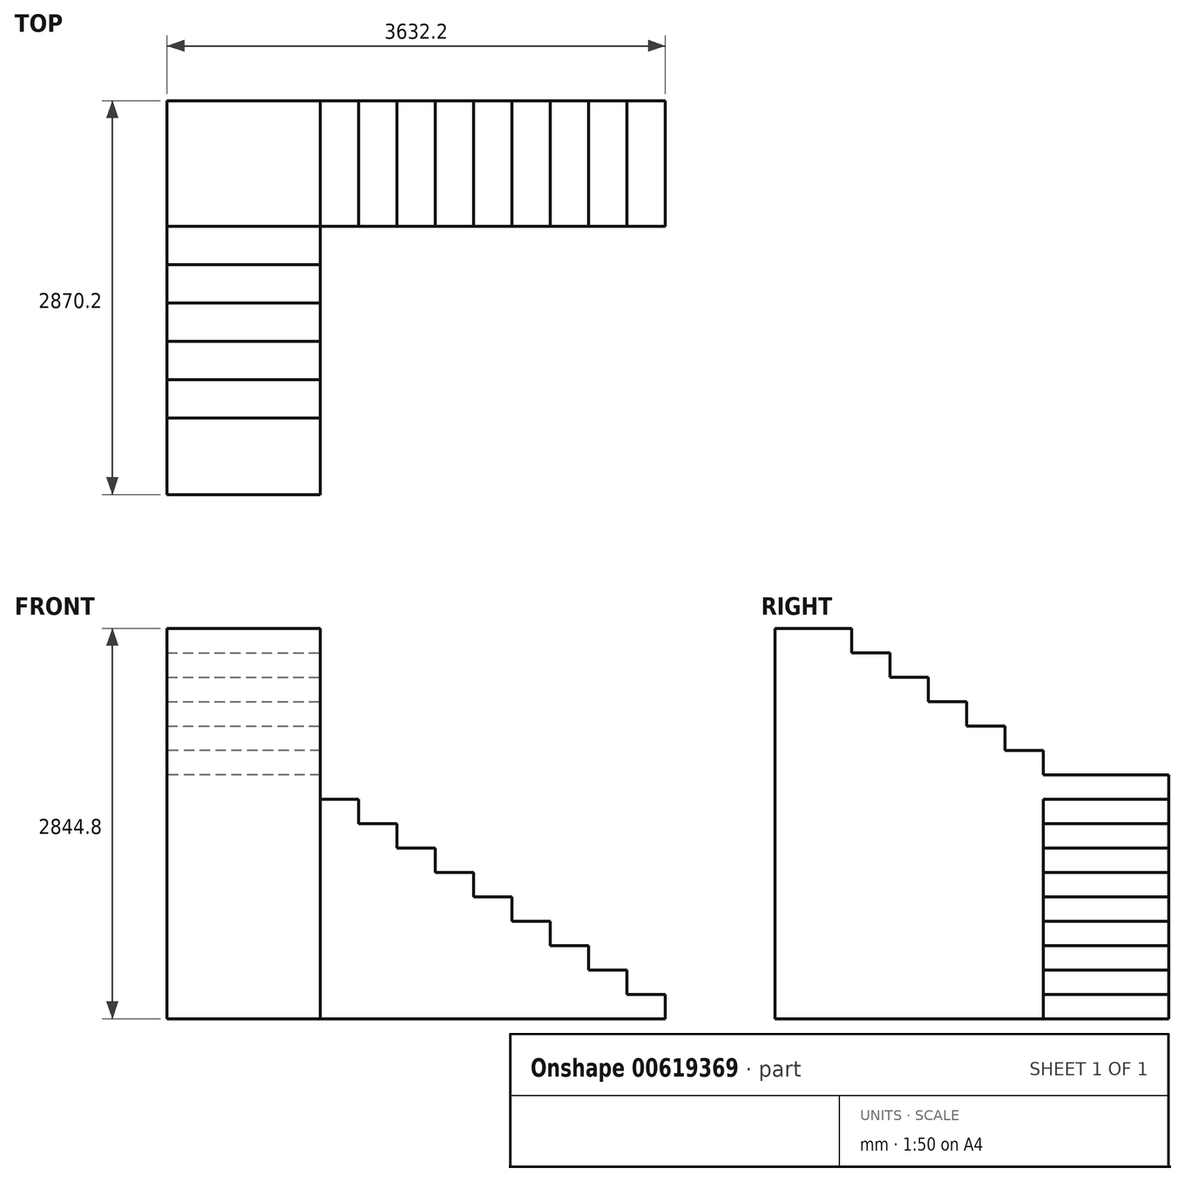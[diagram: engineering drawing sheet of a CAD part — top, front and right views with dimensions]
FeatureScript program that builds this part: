
annotation { "Feature Type Name" : "Feature", "Feature Type Description" : "" }
export const myFeature = defineFeature(function(context is Context, id is Id, definition is map)
    precondition{}
    {
        {
            var Q0;
            Q0=qCreatedBy(makeId("Top.planeOp"),FACE);
            var sketch = newSketch(context, id + "F0", { "sketchPlane" : qUnion([Q0])});
            skLineSegment(sketch, "E0.bottom", {"start": v(0, 0) * mm, "end": v(-2514.6, 0) * mm});
            skLineSegment(sketch, "E0.top", {"start": v(0, 914.4) * mm, "end": v(-2514.6, 914.4) * mm});
            skLineSegment(sketch, "E0.left", {"start": v(0, 0) * mm, "end": v(0, 914.4) * mm});
            skLineSegment(sketch, "E1", {"start": v(-1397, 914.4) * mm, "end": v(-1397, 0) * mm});
            skLineSegment(sketch, "E2", {"start": v(-1955.8, 914.4) * mm, "end": v(-1955.8, 0) * mm});
            skLineSegment(sketch, "E3", {"start": v(-838.2, 914.4) * mm, "end": v(-838.2, 0) * mm});
            skLineSegment(sketch, "E4", {"start": v(-1676.4, 914.4) * mm, "end": v(-1676.4, 0) * mm});
            skLineSegment(sketch, "E5", {"start": v(-279.4, 914.4) * mm, "end": v(-279.4, 0) * mm});
            skLineSegment(sketch, "E6", {"start": v(-1117.6, 914.4) * mm, "end": v(-1117.6, 0) * mm});
            skLineSegment(sketch, "E7", {"start": v(-558.8, 914.4) * mm, "end": v(-558.8, 0) * mm});
            skLineSegment(sketch, "E8", {"start": v(-2235.2, 914.4) * mm, "end": v(-2235.2, 0) * mm});
            skLineSegment(sketch, "E9.bottom", {"start": v(-2514.6, 914.4) * mm, "end": v(-3632.2, 914.4) * mm});
            skLineSegment(sketch, "E9.top", {"start": v(-2514.6, 0) * mm, "end": v(-3632.2, 0) * mm});
            skLineSegment(sketch, "E9.left", {"start": v(-2514.6, 914.4) * mm, "end": v(-2514.6, 0) * mm});
            skLineSegment(sketch, "E9.right", {"start": v(-3632.2, 914.4) * mm, "end": v(-3632.2, 0) * mm});
            skLineSegment(sketch, "E10", {"start": v(-3632.2, 0) * mm, "end": v(-3632.2, -279.4) * mm});
            skLineSegment(sketch, "E11", {"start": v(-3632.2, -279.4) * mm, "end": v(-2514.6, -279.4) * mm});
            skLineSegment(sketch, "E12", {"start": v(-2514.6, -279.4) * mm, "end": v(-2514.6, 0) * mm});
            skLineSegment(sketch, "E13", {"start": v(-3632.2, -279.4) * mm, "end": v(-3632.2, -558.8) * mm});
            skLineSegment(sketch, "E14", {"start": v(-3632.2, -558.8) * mm, "end": v(-2514.6, -558.8) * mm});
            skLineSegment(sketch, "E15", {"start": v(-2514.6, -558.8) * mm, "end": v(-2514.6, -279.4) * mm});
            skLineSegment(sketch, "E16", {"start": v(-3632.2, -558.8) * mm, "end": v(-3632.2, -838.2) * mm});
            skLineSegment(sketch, "E17", {"start": v(-3632.2, -838.2) * mm, "end": v(-2514.6, -838.2) * mm});
            skLineSegment(sketch, "E18", {"start": v(-2514.6, -838.2) * mm, "end": v(-2514.6, -558.8) * mm});
            skLineSegment(sketch, "E19", {"start": v(-3632.2, -838.2) * mm, "end": v(-3632.2, -1117.6) * mm});
            skLineSegment(sketch, "E20", {"start": v(-3632.2, -1117.6) * mm, "end": v(-2514.6, -1117.6) * mm});
            skLineSegment(sketch, "E21", {"start": v(-2514.6, -1117.6) * mm, "end": v(-2514.6, -838.2) * mm});
            skLineSegment(sketch, "E22", {"start": v(-3632.2, -1117.6) * mm, "end": v(-3632.2, -1397) * mm});
            skLineSegment(sketch, "E23", {"start": v(-3632.2, -1397) * mm, "end": v(-2514.6, -1397) * mm});
            skLineSegment(sketch, "E24", {"start": v(-2514.6, -1397) * mm, "end": v(-2514.6, -1117.6) * mm});
            skLineSegment(sketch, "E25", {"start": v(-3632.2, -1397) * mm, "end": v(-3632.2, -1955.8) * mm});
            skLineSegment(sketch, "E26", {"start": v(-3632.2, -1955.8) * mm, "end": v(-2514.6, -1955.8) * mm});
            skLineSegment(sketch, "E27", {"start": v(-2514.6, -1955.8) * mm, "end": v(-2514.6, -1397) * mm});
            skSolve(sketch);
        }
        {
            var Q0;
            {var subQ0=sQuery(id+"F0.wireOp",EDGE,"E0.left");Q0=makeQuery(id+"F0.imprint","IMPRINT",FACE,{"disambiguationData":[TD([[makeQuery(id+"F0.imprint","IMPRINT",EDGE,{"derivedFrom":subQ0}),1.0]])]});}
            extrude(context, id + "F1", {"entities" : qUnion([Q0]), "depth" : 177.8 * mm, "offsetDistance" : 25.4 * mm});
        }
        {
            var Q0;
            {var subQ0=sQuery(id+"F0.wireOp",EDGE,"E5");Q0=makeQuery(id+"F0.imprint","IMPRINT",FACE,{"disambiguationData":[TD([[makeQuery(id+"F0.imprint","IMPRINT",EDGE,{"derivedFrom":subQ0}),-1.0]])]});}
            extrude(context, id + "F2", {"entities" : qUnion([Q0]), "operationType" : NewBodyOperationType.ADD, "depth" : 355.6 * mm, "offsetDistance" : 25.4 * mm});
        }
        {
            var Q0;
            {var subQ0=sQuery(id+"F0.wireOp",EDGE,"E3");Q0=makeQuery(id+"F0.imprint","IMPRINT",FACE,{"disambiguationData":[TD([[makeQuery(id+"F0.imprint","IMPRINT",EDGE,{"derivedFrom":subQ0}),1.0]])]});}
            extrude(context, id + "F3", {"entities" : qUnion([Q0]), "operationType" : NewBodyOperationType.ADD, "depth" : 533.4 * mm, "offsetDistance" : 25.4 * mm});
        }
        {
            var Q0;
            {var subQ0=sQuery(id+"F0.wireOp",EDGE,"E3");Q0=makeQuery(id+"F0.imprint","IMPRINT",FACE,{"disambiguationData":[TD([[makeQuery(id+"F0.imprint","IMPRINT",EDGE,{"derivedFrom":subQ0}),-1.0]])]});}
            extrude(context, id + "F4", {"entities" : qUnion([Q0]), "operationType" : NewBodyOperationType.ADD, "depth" : 711.2 * mm, "offsetDistance" : 25.4 * mm});
        }
        {
            var Q0;
            {var subQ0=sQuery(id+"F0.wireOp",EDGE,"E1");Q0=makeQuery(id+"F0.imprint","IMPRINT",FACE,{"disambiguationData":[TD([[makeQuery(id+"F0.imprint","IMPRINT",EDGE,{"derivedFrom":subQ0}),1.0]])]});}
            extrude(context, id + "F5", {"entities" : qUnion([Q0]), "operationType" : NewBodyOperationType.ADD, "depth" : 889 * mm, "offsetDistance" : 25.4 * mm});
        }
        {
            var Q0;
            {var subQ0=sQuery(id+"F0.wireOp",EDGE,"E1");Q0=makeQuery(id+"F0.imprint","IMPRINT",FACE,{"disambiguationData":[TD([[makeQuery(id+"F0.imprint","IMPRINT",EDGE,{"derivedFrom":subQ0}),-1.0]])]});}
            extrude(context, id + "F6", {"entities" : qUnion([Q0]), "operationType" : NewBodyOperationType.ADD, "depth" : 1066.8 * mm, "offsetDistance" : 25.4 * mm});
        }
        {
            var Q0;
            {var subQ0=sQuery(id+"F0.wireOp",EDGE,"E2");Q0=makeQuery(id+"F0.imprint","IMPRINT",FACE,{"disambiguationData":[TD([[makeQuery(id+"F0.imprint","IMPRINT",EDGE,{"derivedFrom":subQ0}),1.0]])]});}
            extrude(context, id + "F7", {"entities" : qUnion([Q0]), "operationType" : NewBodyOperationType.ADD, "depth" : 1244.6 * mm, "offsetDistance" : 25.4 * mm});
        }
        {
            var Q0;
            {var subQ0=sQuery(id+"F0.wireOp",EDGE,"E2");Q0=makeQuery(id+"F0.imprint","IMPRINT",FACE,{"disambiguationData":[TD([[makeQuery(id+"F0.imprint","IMPRINT",EDGE,{"derivedFrom":subQ0}),-1.0]])]});}
            extrude(context, id + "F8", {"entities" : qUnion([Q0]), "operationType" : NewBodyOperationType.ADD, "depth" : 1422.4 * mm, "offsetDistance" : 25.4 * mm});
        }
        {
            var Q0;
            {var subQ2=sQuery(id+"F0.wireOp",EDGE,"E8");Q0=makeQuery(id+"F0.imprint","IMPRINT",FACE,{"disambiguationData":[TD([[makeQuery(id+"F0.imprint","IMPRINT",EDGE,{"derivedFrom":subQ2}),-1.0]])]});}
            extrude(context, id + "F9", {"entities" : qUnion([Q0]), "operationType" : NewBodyOperationType.ADD, "depth" : 1600.2 * mm, "offsetDistance" : 25.4 * mm});
        }
        {
            var Q0;
            Q0=makeQuery(id+"F0.imprint","IMPRINT",FACE,{"disambiguationData":[TD([[makeQuery(id+"F0.imprint","IMPRINT",EDGE,{"derivedFrom":sQuery(id+"F0.wireOp",EDGE,"E9.bottom")}),1.0]])]});
            extrude(context, id + "F10", {"entities" : qUnion([Q0]), "operationType" : NewBodyOperationType.ADD, "depth" : 1778 * mm, "offsetDistance" : 25.4 * mm});
        }
        {
            var Q0;
            Q0=makeQuery(id+"F0.imprint","IMPRINT",FACE,{"disambiguationData":[TD([[makeQuery(id+"F0.imprint","IMPRINT",EDGE,{"derivedFrom":sQuery(id+"F0.wireOp",EDGE,"E9.top")}),1.0]])]});
            extrude(context, id + "F11", {"entities" : qUnion([Q0]), "operationType" : NewBodyOperationType.ADD, "depth" : 1955.8 * mm, "offsetDistance" : 25.4 * mm});
        }
        {
            var Q0;
            Q0=makeQuery(id+"F0.imprint","IMPRINT",FACE,{"disambiguationData":[TD([[makeQuery(id+"F0.imprint","IMPRINT",EDGE,{"derivedFrom":sQuery(id+"F0.wireOp",EDGE,"E11")}),-1.0]])]});
            extrude(context, id + "F12", {"entities" : qUnion([Q0]), "operationType" : NewBodyOperationType.ADD, "depth" : 2133.6 * mm, "offsetDistance" : 25.4 * mm});
        }
        {
            var Q0;
            Q0=makeQuery(id+"F0.imprint","IMPRINT",FACE,{"disambiguationData":[TD([[makeQuery(id+"F0.imprint","IMPRINT",EDGE,{"derivedFrom":sQuery(id+"F0.wireOp",EDGE,"E14")}),-1.0]])]});
            extrude(context, id + "F13", {"entities" : qUnion([Q0]), "operationType" : NewBodyOperationType.ADD, "depth" : 2311.4 * mm, "offsetDistance" : 25.4 * mm});
        }
        {
            var Q0;
            Q0=makeQuery(id+"F0.imprint","IMPRINT",FACE,{"disambiguationData":[TD([[makeQuery(id+"F0.imprint","IMPRINT",EDGE,{"derivedFrom":sQuery(id+"F0.wireOp",EDGE,"E17")}),-1.0]])]});
            extrude(context, id + "F14", {"entities" : qUnion([Q0]), "operationType" : NewBodyOperationType.ADD, "depth" : 2489.2 * mm, "offsetDistance" : 25.4 * mm});
        }
        {
            var Q0;
            Q0=makeQuery(id+"F0.imprint","IMPRINT",FACE,{"disambiguationData":[TD([[makeQuery(id+"F0.imprint","IMPRINT",EDGE,{"derivedFrom":sQuery(id+"F0.wireOp",EDGE,"E20")}),-1.0]])]});
            extrude(context, id + "F15", {"entities" : qUnion([Q0]), "operationType" : NewBodyOperationType.ADD, "depth" : 2667 * mm, "offsetDistance" : 25.4 * mm});
        }
        {
            var Q0;
            Q0=makeQuery(id+"F0.imprint","IMPRINT",FACE,{"disambiguationData":[TD([[makeQuery(id+"F0.imprint","IMPRINT",EDGE,{"derivedFrom":sQuery(id+"F0.wireOp",EDGE,"E23")}),-1.0]])]});
            extrude(context, id + "F16", {"entities" : qUnion([Q0]), "operationType" : NewBodyOperationType.ADD, "depth" : 2844.8 * mm, "offsetDistance" : 25.4 * mm});
        }
    });
